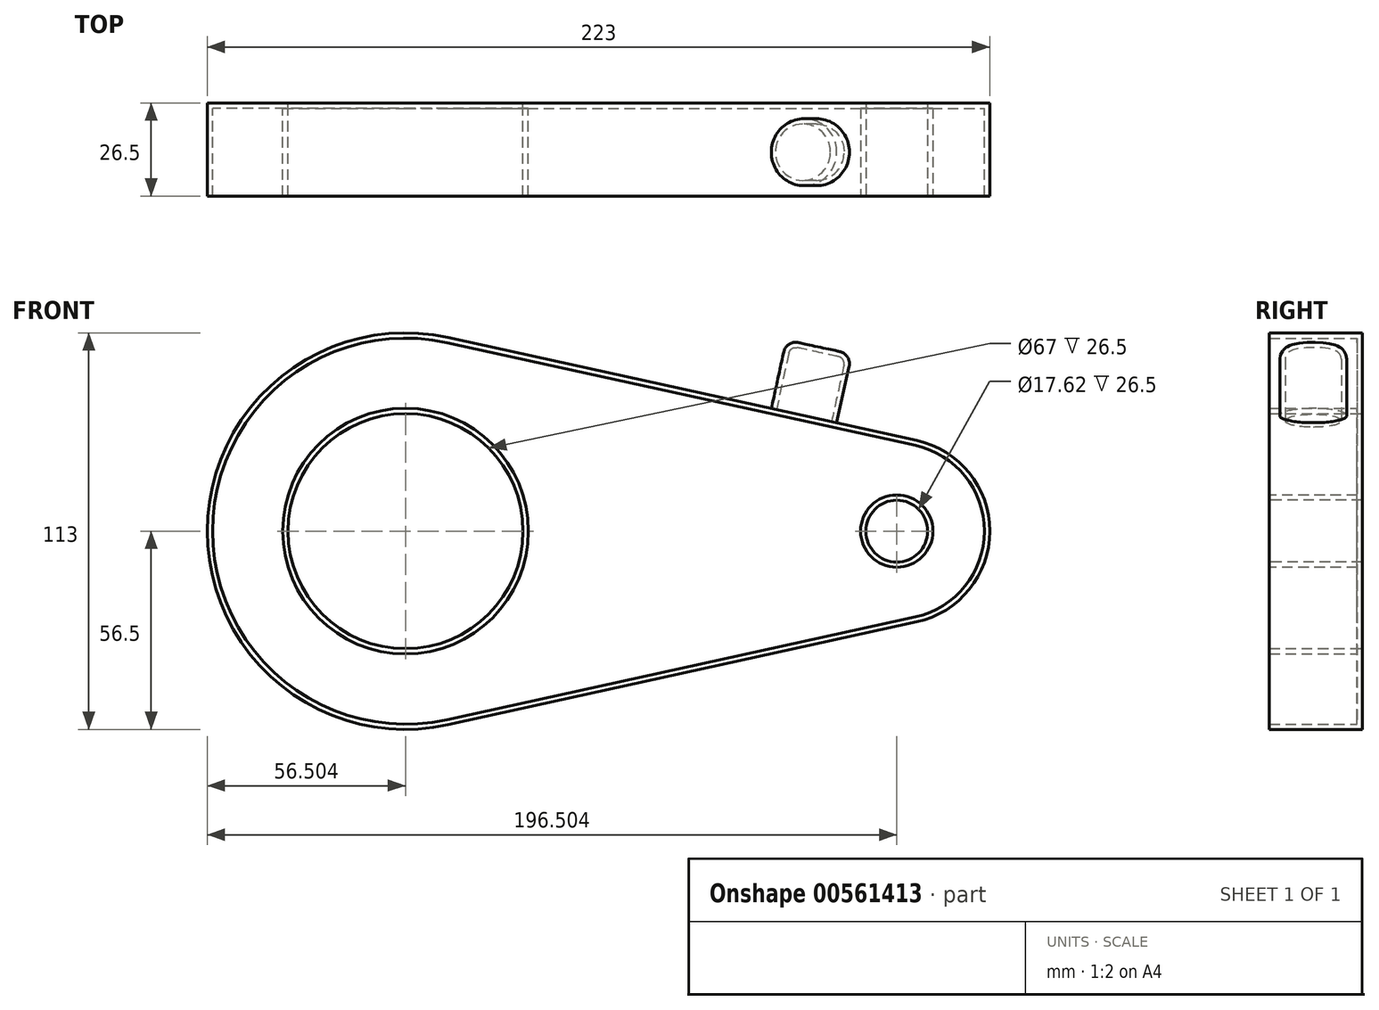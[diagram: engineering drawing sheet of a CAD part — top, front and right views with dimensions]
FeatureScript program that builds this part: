
annotation { "Feature Type Name" : "Feature", "Feature Type Description" : "" }
export const myFeature = defineFeature(function(context is Context, id is Id, definition is map)
    precondition{}
    {
        {
            var Q0;
            Q0=qCreatedBy(makeId("Front.planeOp"),FACE);
            var sketch = newSketch(context, id + "F0", { "sketchPlane" : qUnion([Q0])});
            skCircle(sketch, "E0", {"center": v(-70.45, 0) * mm, "radius": 55 * mm});
            skCircle(sketch, "E1", {"center": v(69.55, 0) * mm, "radius": 25 * mm});
            skLineSegment(sketch, "E2", {"start": v(-58.66, 53.72) * mm, "end": v(74.91, 24.42) * mm});
            skLineSegment(sketch, "E3", {"start": v(-58.66, -53.72) * mm, "end": v(74.91, -24.42) * mm});
            skCircle(sketch, "E4", {"center": v(-70.45, 0) * mm, "radius": 35 * mm});
            skSolve(sketch);
        }
        {
            var Q0;
            Q0 = qSketchRegion(id + "F0", true);
            extrude(context, id + "F1", {"entities" : qUnion([Q0]), "depth" : 25 * mm, "offsetDistance" : 25 * mm});
        }
        {
            var Q0;
            Q0=makeQuery(id+"F1.opExtrude","SWEPT_FACE",FACE,{"disambiguationData":[OSD([sQuery(id+"F0.wireOp",EDGE,"E2")])]});
            var sketch = newSketch(context, id + "F2", { "sketchPlane" : qUnion([Q0])});
            skCircle(sketch, "E5", {"center": v(35.07, -12.5) * mm, "radius": 8.04 * mm});
            skPoint(sketch, "E5.centerSnap0", {"position": v(67.94, -12.5) * mm});
            skSolve(sketch);
        }
        {
            var Q0;
            Q0=makeQuery(id+"F2.imprint","IMPRINT",FACE,{"disambiguationData":[TD([[makeQuery(id+"F2.imprint","IMPRINT",EDGE,{"derivedFrom":sQuery(id+"F2.wireOp",EDGE,"E5")}),1.0]])]});
            extrude(context, id + "F3", {"entities" : qUnion([Q0]), "operationType" : NewBodyOperationType.ADD, "depth" : 20 * mm, "offsetDistance" : 25 * mm});
        }
        {
            var Q0;
            Q0=makeQuery(id+"F3.opExtrude","CAP_FACE",FACE,{"disambiguationData":[OSD([sQuery(id+"F2.wireOp",EDGE,"E5")])],"isStart":false});
            var Q1;
            Q1=makeQuery(id+"F3.opExtrude","CAP_EDGE",EDGE,{"disambiguationData":[OSD([sQuery(id+"F2.wireOp",EDGE,"E5")])],"isStart":true});
            fillet(context, id + "F4", {"entities" : qUnion([Q0, Q1]), "radius" : 2 * mm, "tangentPropagation" : true, "allowEdgeOverflow" : false});
        }
        {
            var Q0;
            Q0=makeQuery(id+"F1.opExtrude","CAP_FACE",FACE,{"disambiguationData":[OSD([sQuery(id+"F0.wireOp",EDGE,"E0"),sQuery(id+"F0.wireOp",EDGE,"E1"),sQuery(id+"F0.wireOp",EDGE,"E2"),sQuery(id+"F0.wireOp",EDGE,"E3"),sQuery(id+"F0.wireOp",EDGE,"E4")])],"isStart":false});
            var sketch = newSketch(context, id + "F5", { "sketchPlane" : qUnion([Q0])});
            skCircle(sketch, "E6", {"center": v(69.55, 0) * mm, "radius": 10.3 * mm});
            skSolve(sketch);
        }
        {
            var Q0;
            Q0=makeQuery(id+"F5.imprint","IMPRINT",FACE,{"disambiguationData":[TD([[makeQuery(id+"F5.imprint","IMPRINT",EDGE,{"derivedFrom":sQuery(id+"F5.wireOp",EDGE,"E6")}),1.0]])]});
            extrude(context, id + "F6", {"entities" : qUnion([Q0]), "operationType" : NewBodyOperationType.REMOVE, "endBound" : BoundingType.THROUGH_ALL, "oppositeDirection" : true, "depth" : 25 * mm, "offsetDistance" : 25 * mm});
        }
        {
            var Q0;
            Q0=makeQuery(id+"F1.opExtrude","CAP_FACE",FACE,{"disambiguationData":[OSD([sQuery(id+"F0.wireOp",EDGE,"E0"),sQuery(id+"F0.wireOp",EDGE,"E1"),sQuery(id+"F0.wireOp",EDGE,"E2"),sQuery(id+"F0.wireOp",EDGE,"E3"),sQuery(id+"F0.wireOp",EDGE,"E4")])],"isStart":false});
            shell(context, id + "F7", {"entities" : qUnion([Q0]), "thickness" : 1.5 * mm, "oppositeDirection" : true});
        }
    });
